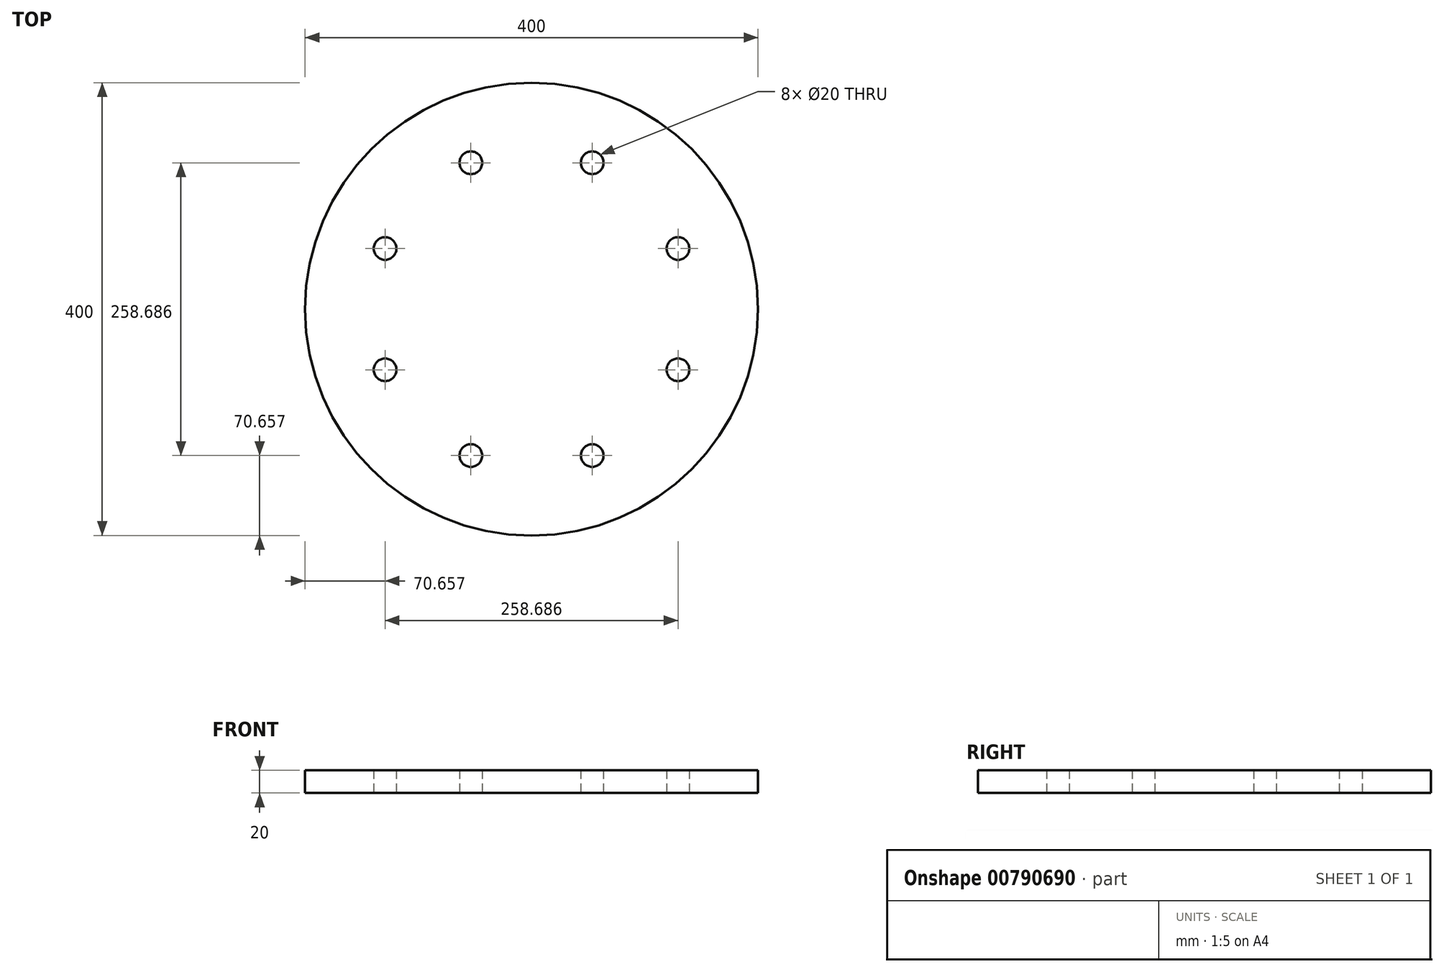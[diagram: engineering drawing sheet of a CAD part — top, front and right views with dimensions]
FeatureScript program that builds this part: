
annotation { "Feature Type Name" : "Feature", "Feature Type Description" : "" }
export const myFeature = defineFeature(function(context is Context, id is Id, definition is map)
    precondition{}
    {
        {
            var Q0;
            Q0=qCreatedBy(makeId("Top.planeOp"),FACE);
            var sketch = newSketch(context, id + "F0", { "sketchPlane" : qUnion([Q0])});
            skCircle(sketch, "E0", {"center": v(0, 0) * mm, "radius": 200 * mm});
            skLineSegment(sketch, "E1", {"start": v(0, 0) * mm, "end": v(0, 140) * mm});
            skLineSegment(sketch, "E2", {"start": v(0, 0) * mm, "end": v(53.58, 129.34) * mm});
            skCircle(sketch, "E3", {"center": v(53.58, 129.34) * mm, "radius": 10 * mm});
            skCircle(sketch, "E4.1.0", {"center": v(-53.58, 129.34) * mm, "radius": 10 * mm});
            skCircle(sketch, "E4.2.0", {"center": v(-129.34, 53.58) * mm, "radius": 10 * mm});
            skCircle(sketch, "E4.3.0", {"center": v(-129.34, -53.58) * mm, "radius": 10 * mm});
            skCircle(sketch, "E4.4.0", {"center": v(-53.58, -129.34) * mm, "radius": 10 * mm});
            skCircle(sketch, "E4.5.0", {"center": v(53.58, -129.34) * mm, "radius": 10 * mm});
            skCircle(sketch, "E4.6.0", {"center": v(129.34, -53.58) * mm, "radius": 10 * mm});
            skCircle(sketch, "E4.7.0", {"center": v(129.34, 53.58) * mm, "radius": 10 * mm});
            skSolve(sketch);
        }
        {
            var Q0;
            Q0=makeQuery(id+"F0.imprint","IMPRINT",FACE,{"disambiguationData":[TD([[makeQuery(id+"F0.imprint","IMPRINT",EDGE,{"derivedFrom":sQuery(id+"F0.wireOp",EDGE,"TMvq6v6R-sMxV-a4da-dBYP-9eOm5g6FeLvq.bottom")}),1.0]])]});
            var Q1;
            Q1=makeQuery(id+"F0.imprint","IMPRINT",FACE,{"disambiguationData":[TD([[makeQuery(id+"F0.imprint","IMPRINT",EDGE,{"derivedFrom":sQuery(id+"F0.wireOp",EDGE,"49d5edba-6f73-482f-bc94-dd4746af2190.1.0.1")}),1.0]])]});
            var Q2;
            Q2=makeQuery(id+"F0.imprint","IMPRINT",FACE,{"disambiguationData":[TD([[makeQuery(id+"F0.imprint","IMPRINT",EDGE,{"derivedFrom":sQuery(id+"F0.wireOp",EDGE,"E0")}),1.0]])]});
            extrude(context, id + "F1", {"entities" : qUnion([Q0, Q1, Q2]), "depth" : 20 * mm, "offsetDistance" : 25 * mm});
        }
    });
